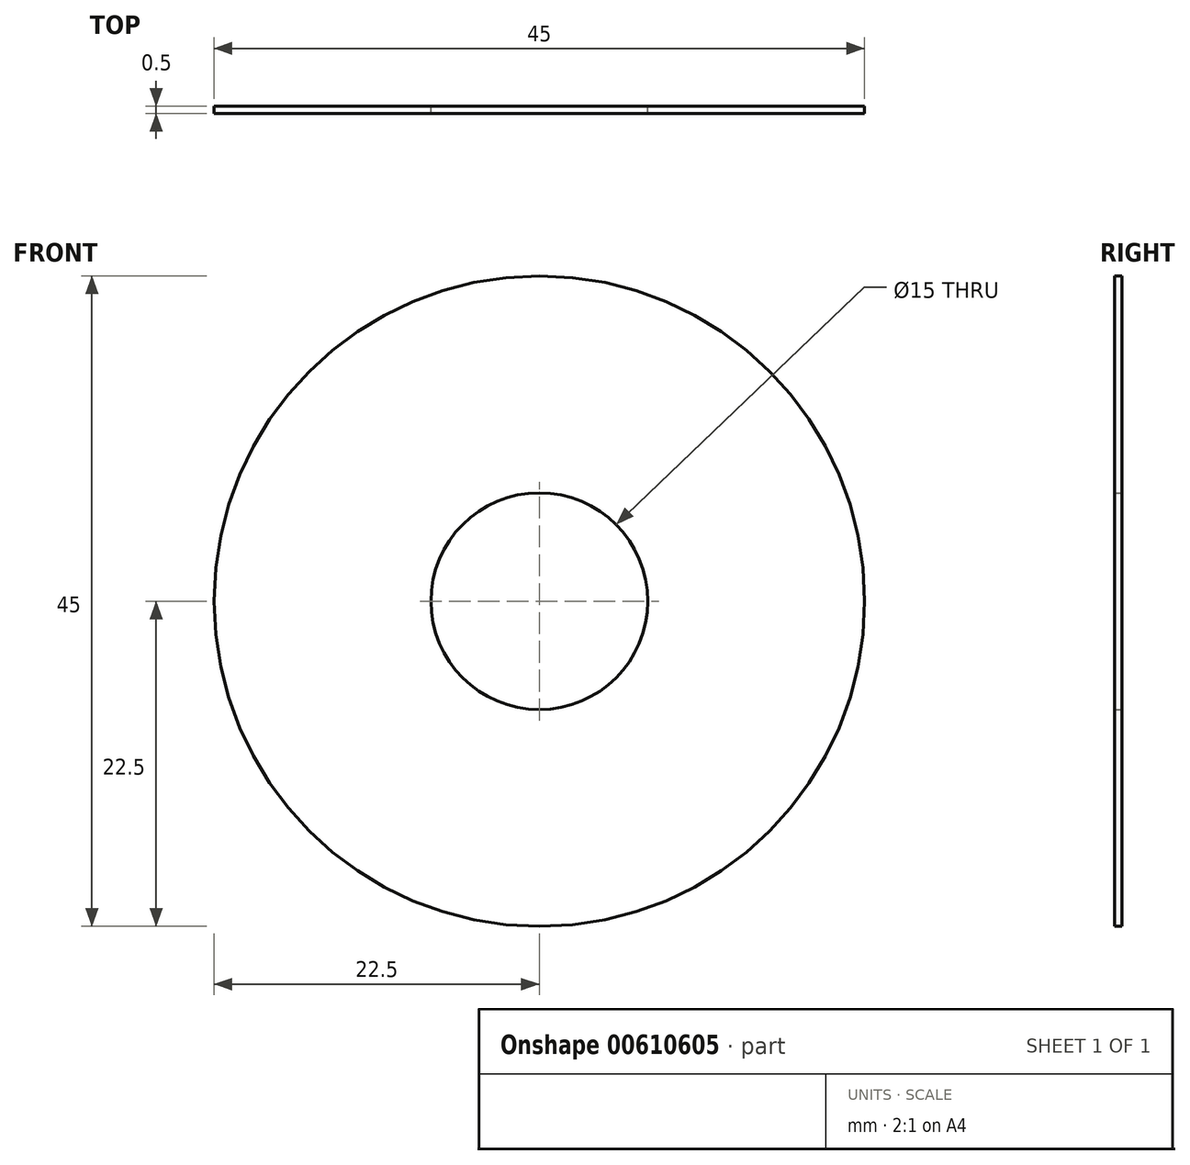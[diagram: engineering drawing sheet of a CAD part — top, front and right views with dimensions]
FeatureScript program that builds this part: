
annotation { "Feature Type Name" : "Feature", "Feature Type Description" : "" }
export const myFeature = defineFeature(function(context is Context, id is Id, definition is map)
    precondition{}
    {
        {
            var Q0;
            Q0=qCreatedBy(makeId("Front.planeOp"),FACE);
            var sketch = newSketch(context, id + "F0", { "sketchPlane" : qUnion([Q0])});
            skCircle(sketch, "E0", {"center": v(0, 0) * mm, "radius": 22.5 * mm});
            skSolve(sketch);
        }
        {
            var Q0;
            Q0=makeQuery(id+"F0.imprint","IMPRINT",FACE,{"disambiguationData":[TD([[makeQuery(id+"F0.imprint","IMPRINT",EDGE,{"derivedFrom":sQuery(id+"F0.wireOp",EDGE,"E0")}),1.0]])]});
            var sketch = newSketch(context, id + "F1", { "sketchPlane" : qUnion([Q0])});
            skCircle(sketch, "E1", {"center": v(0, 0) * mm, "radius": 7.5 * mm});
            skSolve(sketch);
        }
        {
            var Q0;
            Q0=makeQuery(id+"F1.imprint","IMPRINT",FACE,{"disambiguationData":[TD([[makeQuery(id+"F1.imprint","IMPRINT",EDGE,{"derivedFrom":sQuery(id+"F1.wireOp",EDGE,"E1")}),-1.0]])]});
            extrude(context, id + "F2", {"entities" : qUnion([Q0]), "depth" : 0.5 * mm, "offsetDistance" : 25 * mm});
        }
    });
